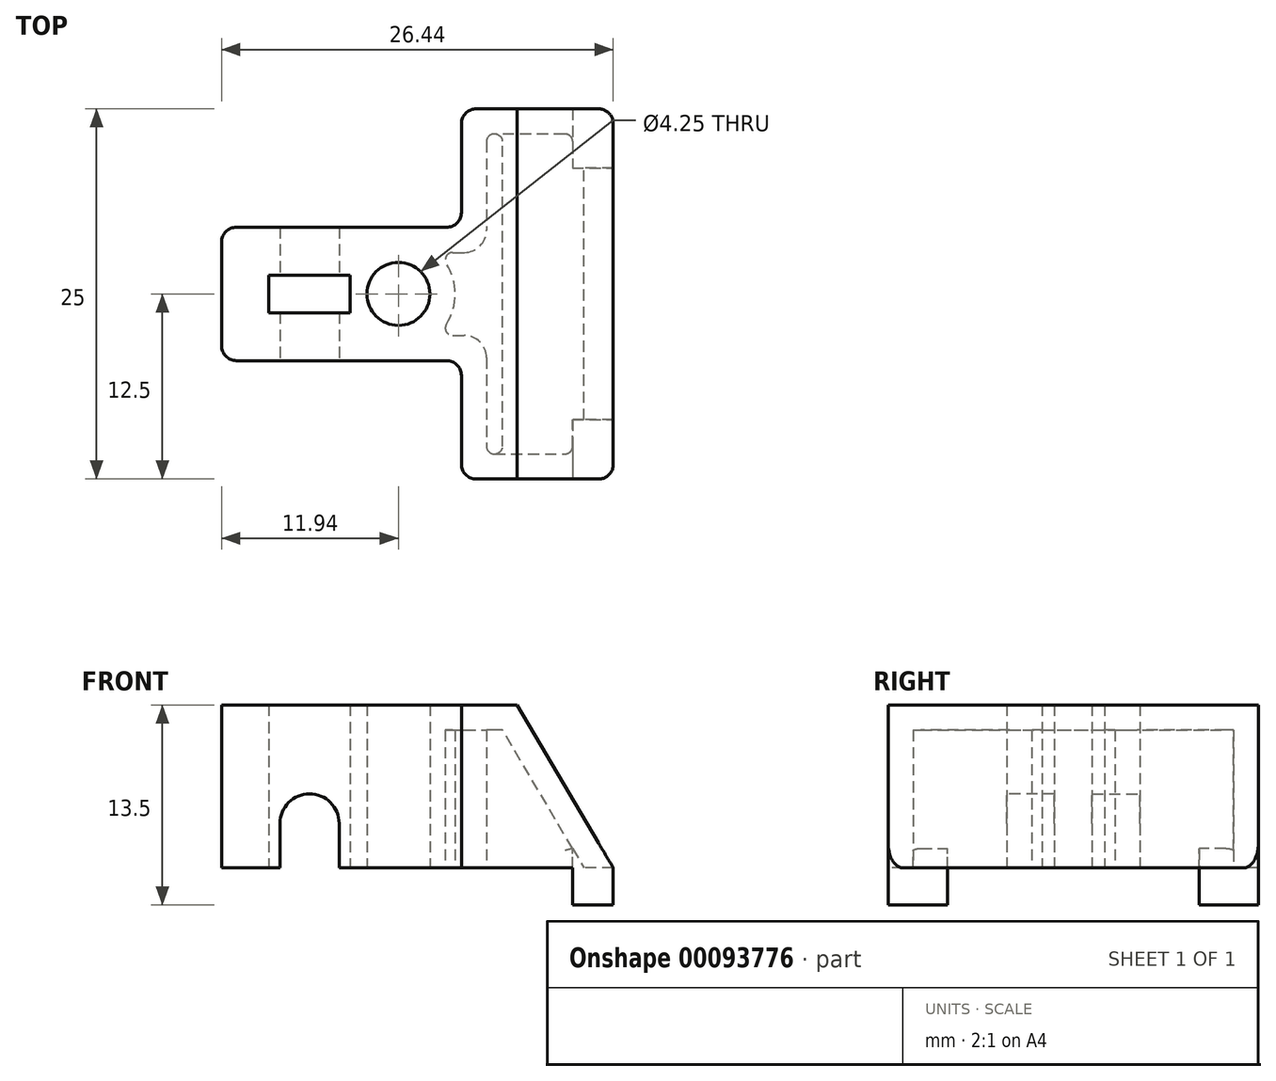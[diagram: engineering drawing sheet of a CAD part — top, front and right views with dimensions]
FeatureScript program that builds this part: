
annotation { "Feature Type Name" : "Feature", "Feature Type Description" : "" }
export const myFeature = defineFeature(function(context is Context, id is Id, definition is map)
    precondition{}
    {
        {
            var Q0;
            Q0=qCreatedBy(makeId("Top.planeOp"),FACE);
            var sketch = newSketch(context, id + "F0", { "sketchPlane" : qUnion([Q0])});
            skCircle(sketch, "E0", {"center": v(0, 0) * mm, "radius": 2.12 * mm});
            skLineSegment(sketch, "E1.bottom", {"start": v(-3.25, 1.27) * mm, "end": v(-8.75, 1.27) * mm});
            skLineSegment(sketch, "E1.top", {"start": v(-3.25, -1.27) * mm, "end": v(-8.75, -1.27) * mm});
            skLineSegment(sketch, "E1.left", {"start": v(-3.25, 1.27) * mm, "end": v(-3.25, -1.27) * mm});
            skLineSegment(sketch, "E1.right", {"start": v(-8.75, 1.27) * mm, "end": v(-8.75, -1.27) * mm});
            skPoint(sketch, "E1.middle", {"position": v(-6, 0) * mm});
            skLineSegment(sketch, "E2.bottom", {"start": v(-8, 4.5) * mm, "end": v(-4, 4.5) * mm});
            skLineSegment(sketch, "E2.top", {"start": v(-8, -4.5) * mm, "end": v(-4, -4.5) * mm});
            skLineSegment(sketch, "E2.left", {"start": v(-8, 4.5) * mm, "end": v(-8, -4.5) * mm});
            skLineSegment(sketch, "E2.right", {"start": v(-4, 4.5) * mm, "end": v(-4, -4.5) * mm});
            skLineSegment(sketch, "E3.bottom", {"start": v(-11.94, 4.5) * mm, "end": v(11.75, 4.5) * mm});
            skLineSegment(sketch, "E3.top", {"start": v(-11.94, -4.5) * mm, "end": v(11.75, -4.5) * mm});
            skLineSegment(sketch, "E3.left", {"start": v(-11.94, 4.5) * mm, "end": v(-11.94, -4.5) * mm});
            skLineSegment(sketch, "E3.right", {"start": v(11.75, 4.5) * mm, "end": v(11.75, -4.5) * mm});
            skLineSegment(sketch, "E4.bottom", {"start": v(11.75, 12.5) * mm, "end": v(4.25, 12.5) * mm});
            skLineSegment(sketch, "E4.top", {"start": v(11.75, -12.5) * mm, "end": v(4.25, -12.5) * mm});
            skLineSegment(sketch, "E4.left", {"start": v(11.75, 12.5) * mm, "end": v(11.75, -12.5) * mm});
            skLineSegment(sketch, "E4.right", {"start": v(4.25, 12.5) * mm, "end": v(4.25, -12.5) * mm});
            skPoint(sketch, "E4.middle", {"position": v(8, 0) * mm});
            skSolve(sketch);
        }
        {
            var Q0;
            {var subQ5=sQuery(id+"F0.wireOp",EDGE,"E4.bottom");Q0=makeQuery(id+"F0.imprint","IMPRINT",FACE,{"disambiguationData":[TD([[makeQuery(id+"F0.imprint","IMPRINT",EDGE,{"derivedFrom":subQ5}),1.0]])]});}
            var Q1;
            {var subQ0=sQuery(id+"F0.wireOp",EDGE,"E4.left");var subQ1=sQuery(id+"F0.wireOp",EDGE,"E3.bottom");var subQ2=makeQuery(id+"F0.imprint","INTERSECT",VERTEX,{"derivedFrom":[subQ1,subQ0]});Q1=makeQuery(id+"F0.imprint","IMPRINT",FACE,{"disambiguationData":[TD([[makeQuery(id+"F0.imprint","IMPRINT",EDGE,{"disambiguationData":[TD([[subQ2,1.0]])],"derivedFrom":subQ1}),-1.0]])]});}
            var Q2;
            {var subQ5=sQuery(id+"F0.wireOp",EDGE,"E4.top");Q2=makeQuery(id+"F0.imprint","IMPRINT",FACE,{"disambiguationData":[TD([[makeQuery(id+"F0.imprint","IMPRINT",EDGE,{"derivedFrom":subQ5}),-1.0]])]});}
            var Q3;
            Q3=makeQuery(id+"F0.imprint","IMPRINT",FACE,{"disambiguationData":[TD([[makeQuery(id+"F0.imprint","IMPRINT",EDGE,{"derivedFrom":sQuery(id+"F0.wireOp",EDGE,"E0")}),-1.0]])]});
            var Q4;
            {var subQ6=sQuery(id+"F0.wireOp",EDGE,"E1.right");Q4=makeQuery(id+"F0.imprint","IMPRINT",FACE,{"disambiguationData":[TD([[makeQuery(id+"F0.imprint","IMPRINT",EDGE,{"derivedFrom":subQ6}),-1.0]])]});}
            var Q5;
            {var subQ0=sQuery(id+"F0.wireOp",EDGE,"E2.right");var subQ1=sQuery(id+"F0.wireOp",EDGE,"E1.bottom");var subQ2=makeQuery(id+"F0.imprint","INTERSECT",VERTEX,{"derivedFrom":[subQ1,subQ0]});Q5=makeQuery(id+"F0.imprint","IMPRINT",FACE,{"disambiguationData":[TD([[makeQuery(id+"F0.imprint","IMPRINT",EDGE,{"disambiguationData":[TD([[subQ2,-1.0]])],"derivedFrom":subQ1}),-1.0]])]});}
            var Q6;
            {var subQ0=sQuery(id+"F0.wireOp",EDGE,"E2.right");var subQ1=sQuery(id+"F0.wireOp",EDGE,"E1.top");var subQ2=makeQuery(id+"F0.imprint","INTERSECT",VERTEX,{"derivedFrom":[subQ1,subQ0]});Q6=makeQuery(id+"F0.imprint","IMPRINT",FACE,{"disambiguationData":[TD([[makeQuery(id+"F0.imprint","IMPRINT",EDGE,{"disambiguationData":[TD([[subQ2,-1.0]])],"derivedFrom":subQ1}),1.0]])]});}
            extrude(context, id + "F1", {"entities" : qUnion([Q0, Q1, Q2, Q3, Q4, Q5, Q6]), "depth" : 11 * mm});
        }
        {
            var Q0;
            {var subQ0=sQuery(id+"F0.wireOp",EDGE,"E2.right");var subQ1=sQuery(id+"F0.wireOp",EDGE,"E1.bottom");var subQ2=makeQuery(id+"F0.imprint","INTERSECT",VERTEX,{"derivedFrom":[subQ1,subQ0]});Q0=makeQuery(id+"F0.imprint","IMPRINT",FACE,{"disambiguationData":[TD([[makeQuery(id+"F0.imprint","IMPRINT",EDGE,{"disambiguationData":[TD([[subQ2,-1.0]])],"derivedFrom":subQ1}),-1.0]])]});}
            var Q1;
            {var subQ0=sQuery(id+"F0.wireOp",EDGE,"E2.right");var subQ1=sQuery(id+"F0.wireOp",EDGE,"E1.top");var subQ2=makeQuery(id+"F0.imprint","INTERSECT",VERTEX,{"derivedFrom":[subQ1,subQ0]});Q1=makeQuery(id+"F0.imprint","IMPRINT",FACE,{"disambiguationData":[TD([[makeQuery(id+"F0.imprint","IMPRINT",EDGE,{"disambiguationData":[TD([[subQ2,-1.0]])],"derivedFrom":subQ1}),1.0]])]});}
            extrude(context, id + "F2", {"entities" : qUnion([Q0, Q1]), "operationType" : NewBodyOperationType.REMOVE, "depth" : 5 * mm});
        }
        {
            var Q0;
            {var subQ0=sQuery(id+"F0.wireOp",EDGE,"E4.right");var subQ1=sQuery(id+"F0.wireOp",EDGE,"E4.bottom");var subQ2=sQuery(id+"F0.wireOp",EDGE,"E3.bottom");var subQ3=sQuery(id+"F0.wireOp",EDGE,"E4.top");var subQ4=sQuery(id+"F0.wireOp",EDGE,"E3.top");var subQ5=sQuery(id+"F0.wireOp",EDGE,"E0");var subQ6=sQuery(id+"F0.wireOp",EDGE,"E1.bottom");var subQ7=sQuery(id+"F0.wireOp",EDGE,"E1.top");var subQ8=sQuery(id+"F0.wireOp",EDGE,"E4.left");var subQ9=sQuery(id+"F0.wireOp",EDGE,"E1.left");Q0=makeQuery(id+"F2.boolean.opBoolean","SPLIT",FACE,{"disambiguationData":[TD([makeQuery(id+"F1.opExtrude","SWEPT_FACE",FACE,{"disambiguationData":[OSD([subQ5])]})])],"derivedFrom":makeQuery(id+"F1.opExtrude","CAP_FACE",FACE,{"disambiguationData":[OSD([subQ5,subQ6,subQ7,subQ9,sQuery(id+"F0.wireOp",EDGE,"E1.right"),subQ2,subQ4,sQuery(id+"F0.wireOp",EDGE,"E3.left"),subQ1,subQ3,subQ8,subQ0])],"isStart":true})});}
            var sketch = newSketch(context, id + "F3", { "sketchPlane" : qUnion([Q0])});
            skLineSegment(sketch, "E5.bottom", {"start": v(11.75, -12.5) * mm, "end": v(14.5, -12.5) * mm});
            skLineSegment(sketch, "E5.top", {"start": v(11.75, -8.5) * mm, "end": v(14.5, -8.5) * mm});
            skLineSegment(sketch, "E5.left", {"start": v(11.75, -12.5) * mm, "end": v(11.75, -8.5) * mm});
            skLineSegment(sketch, "E5.right", {"start": v(14.5, -12.5) * mm, "end": v(14.5, -8.5) * mm});
            skLineSegment(sketch, "E6", {"start": v(0, 0) * mm, "end": v(11.75, 0) * mm});
            skLineSegment(sketch, "E7.MirrorCS", {"start": v(11.75, 8.5) * mm, "end": v(14.5, 8.5) * mm});
            skLineSegment(sketch, "E8.MirrorCS", {"start": v(14.5, 12.5) * mm, "end": v(14.5, 8.5) * mm});
            skLineSegment(sketch, "E9.MirrorCS", {"start": v(11.75, 12.5) * mm, "end": v(14.5, 12.5) * mm});
            skLineSegment(sketch, "E10.MirrorCS", {"start": v(11.75, 12.5) * mm, "end": v(11.75, 8.5) * mm});
            skSolve(sketch);
        }
        {
            var Q0;
            {var subQ0=sQuery(id+"F0.wireOp",EDGE,"E2.right");Q0=makeQuery(id+"F2.boolean.opBoolean","COPY",EDGE,{"derivedFrom":makeQuery(id+"F2.opExtrude","CAP_EDGE",EDGE,{"disambiguationData":[OSD([subQ0]),TDD([makeQuery(id+"F0.imprint","IMPRINT",EDGE,{"disambiguationData":[TD([[makeQuery(id+"F0.imprint","INTERSECT",VERTEX,{"derivedFrom":[subQ0,sQuery(id+"F0.wireOp",EDGE,"E3.bottom")]}),-1.0]])],"derivedFrom":subQ0})])],"isStart":false})});}
            var Q1;
            {var subQ0=sQuery(id+"F0.wireOp",EDGE,"E2.left");Q1=makeQuery(id+"F2.boolean.opBoolean","COPY",EDGE,{"derivedFrom":makeQuery(id+"F2.opExtrude","CAP_EDGE",EDGE,{"disambiguationData":[OSD([subQ0]),TDD([makeQuery(id+"F0.imprint","IMPRINT",EDGE,{"disambiguationData":[TD([[makeQuery(id+"F0.imprint","INTERSECT",VERTEX,{"derivedFrom":[subQ0,sQuery(id+"F0.wireOp",EDGE,"E3.bottom")]}),-1.0]])],"derivedFrom":subQ0})])],"isStart":false})});}
            var Q2;
            {var subQ0=sQuery(id+"F0.wireOp",EDGE,"E2.left");Q2=makeQuery(id+"F2.boolean.opBoolean","COPY",EDGE,{"derivedFrom":makeQuery(id+"F2.opExtrude","CAP_EDGE",EDGE,{"disambiguationData":[OSD([subQ0]),TDD([makeQuery(id+"F0.imprint","IMPRINT",EDGE,{"disambiguationData":[TD([[makeQuery(id+"F0.imprint","INTERSECT",VERTEX,{"derivedFrom":[subQ0,sQuery(id+"F0.wireOp",EDGE,"E3.top")]}),1.0]])],"derivedFrom":subQ0})])],"isStart":false})});}
            var Q3;
            {var subQ0=sQuery(id+"F0.wireOp",EDGE,"E2.right");Q3=makeQuery(id+"F2.boolean.opBoolean","COPY",EDGE,{"derivedFrom":makeQuery(id+"F2.opExtrude","CAP_EDGE",EDGE,{"disambiguationData":[OSD([subQ0]),TDD([makeQuery(id+"F0.imprint","IMPRINT",EDGE,{"disambiguationData":[TD([[makeQuery(id+"F0.imprint","INTERSECT",VERTEX,{"derivedFrom":[subQ0,sQuery(id+"F0.wireOp",EDGE,"E3.top")]}),1.0]])],"derivedFrom":subQ0})])],"isStart":false})});}
            fillet(context, id + "F4", {"entities" : qUnion([Q0, Q1, Q2, Q3]), "radius" : 2 * mm, "tangentPropagation" : true, "allowEdgeOverflow" : false});
        }
        {
            var Q0;
            Q0=makeQuery(id+"F3.imprint","IMPRINT",FACE,{"disambiguationData":[TD([[makeQuery(id+"F3.imprint","IMPRINT",EDGE,{"derivedFrom":sQuery(id+"F3.wireOp",EDGE,"E5.bottom")}),1.0]])]});
            var Q1;
            Q1=makeQuery(id+"F3.imprint","IMPRINT",FACE,{"disambiguationData":[TD([[makeQuery(id+"F3.imprint","IMPRINT",EDGE,{"derivedFrom":sQuery(id+"F3.wireOp",EDGE,"E7.MirrorCS")}),1.0]])]});
            extrude(context, id + "F5", {"entities" : qUnion([Q0, Q1]), "operationType" : NewBodyOperationType.ADD, "depth" : 5 * mm, "symmetric" : true});
        }
        {
            var Q0;
            Q0=makeQuery(id+"F5.boolean.opBoolean","MERGE",FACE,{"derivedFrom":[makeQuery(id+"F1.opExtrude","SWEPT_FACE",FACE,{"disambiguationData":[OSD([sQuery(id+"F0.wireOp",EDGE,"E4.bottom")])]}),makeQuery(id+"F5.opExtrude","SWEPT_FACE",FACE,{"disambiguationData":[OSD([sQuery(id+"F3.wireOp",EDGE,"E5.bottom")])]})]});
            var sketch = newSketch(context, id + "F6", { "sketchPlane" : qUnion([Q0])});
            skLineSegment(sketch, "E11", {"start": v(-11.75, 0) * mm, "end": v(-14.5, 0) * mm});
            skLineSegment(sketch, "E12", {"start": v(-14.5, 0) * mm, "end": v(-8, 11) * mm});
            skSolve(sketch);
        }
        {
            var Q0;
            {var subQ0=sQuery(id+"F6.wireOp",EDGE,"E12");var subQ1=sQuery(id+"F0.wireOp",EDGE,"E4.bottom");var subQ2=makeQuery(id+"F1.opExtrude","CAP_EDGE",EDGE,{"disambiguationData":[OSD([subQ1])],"isStart":false});var subQ3=makeQuery(id+"F6.imprint","INTERSECT",VERTEX,{"derivedFrom":[subQ2,subQ0]});Q0=makeQuery(id+"F6.imprint","IMPRINT",FACE,{"disambiguationData":[TD([[makeQuery(id+"F6.imprint","IMPRINT",EDGE,{"disambiguationData":[TD([[subQ3,1.0]])],"derivedFrom":subQ0}),1.0]])]});}
            var Q1;
            {var subQ0=sQuery(id+"F6.wireOp",EDGE,"E12");var subQ1=sQuery(id+"F3.wireOp",EDGE,"E5.bottom");var subQ4=makeQuery(id+"F5.opExtrude","CAP_EDGE",EDGE,{"disambiguationData":[OSD([subQ1])],"isStart":true});var subQ5=makeQuery(id+"F6.imprint","INTERSECT",VERTEX,{"derivedFrom":[subQ4,subQ0]});Q1=makeQuery(id+"F6.imprint","IMPRINT",FACE,{"disambiguationData":[TD([[makeQuery(id+"F6.imprint","IMPRINT",EDGE,{"disambiguationData":[TD([[subQ5,-1.0]])],"derivedFrom":subQ4}),1.0]])]});}
            extrude(context, id + "F7", {"entities" : qUnion([Q0, Q1]), "operationType" : NewBodyOperationType.REMOVE, "endBound" : BoundingType.THROUGH_ALL, "oppositeDirection" : true, "depth" : 25 * mm});
        }
        {
            var Q0;
            {var subQ0=sQuery(id+"F6.wireOp",EDGE,"E12");var subQ1=makeQuery(id+"F5.opExtrude","CAP_EDGE",EDGE,{"disambiguationData":[OSD([sQuery(id+"F3.wireOp",EDGE,"E5.bottom")])],"isStart":true});var subQ2=makeQuery(id+"F6.imprint","INTERSECT",VERTEX,{"derivedFrom":[subQ1,subQ0]});Q0=makeQuery(id+"F6.imprint","IMPRINT",FACE,{"disambiguationData":[TD([[makeQuery(id+"F6.imprint","IMPRINT",EDGE,{"disambiguationData":[TD([[subQ2,-1.0]])],"derivedFrom":subQ0}),-1.0]])]});}
            var Q1;
            {var subQ7=sQuery(id+"F6.wireOp",EDGE,"E11");Q1=makeQuery(id+"F6.imprint","IMPRINT",FACE,{"disambiguationData":[TD([[makeQuery(id+"F6.imprint","IMPRINT",EDGE,{"derivedFrom":subQ7}),-1.0]])]});}
            var Q2;
            Q2=makeQuery(id+"F5.boolean.opBoolean","MERGE",FACE,{"derivedFrom":[makeQuery(id+"F1.opExtrude","SWEPT_FACE",FACE,{"disambiguationData":[OSD([sQuery(id+"F0.wireOp",EDGE,"E4.top")])]}),makeQuery(id+"F5.opExtrude","SWEPT_FACE",FACE,{"disambiguationData":[OSD([sQuery(id+"F3.wireOp",EDGE,"E9.MirrorCS")])]})]});
            extrude(context, id + "F8", {"entities" : qUnion([Q0, Q1]), "operationType" : NewBodyOperationType.ADD, "endBound" : BoundingType.UP_TO_SURFACE, "oppositeDirection" : true, "endBoundEntityFace" : qUnion([Q2]), "depth" : 25 * mm});
        }
        {
            var Q0;
            {var subQ0=sQuery(id+"F0.wireOp",EDGE,"E4.bottom");var subQ1=sQuery(id+"F0.wireOp",EDGE,"E4.right");var subQ2=sQuery(id+"F0.wireOp",EDGE,"E3.bottom");var subQ3=sQuery(id+"F0.wireOp",EDGE,"E4.left");var subQ4=sQuery(id+"F0.wireOp",EDGE,"E3.top");var subQ5=sQuery(id+"F0.wireOp",EDGE,"E4.top");var subQ6=sQuery(id+"F0.wireOp",EDGE,"E0");var subQ7=sQuery(id+"F0.wireOp",EDGE,"E1.left");var subQ8=sQuery(id+"F0.wireOp",EDGE,"E1.bottom");var subQ9=sQuery(id+"F0.wireOp",EDGE,"E1.top");Q0=makeQuery(id+"F8.boolean.opBoolean","MERGE",FACE,{"derivedFrom":[makeQuery(id+"F2.boolean.opBoolean","SPLIT",FACE,{"disambiguationData":[TD([makeQuery(id+"F1.opExtrude","SWEPT_FACE",FACE,{"disambiguationData":[OSD([subQ6])]})])],"derivedFrom":makeQuery(id+"F1.opExtrude","CAP_FACE",FACE,{"disambiguationData":[OSD([subQ6,subQ8,subQ9,subQ7,sQuery(id+"F0.wireOp",EDGE,"E1.right"),subQ2,subQ4,sQuery(id+"F0.wireOp",EDGE,"E3.left"),subQ0,subQ5,subQ3,subQ1])],"isStart":true})}),makeQuery(id+"F8.opExtrude","SWEPT_FACE",FACE,{"disambiguationData":[OSD([subQ0,sQuery(id+"F6.wireOp",EDGE,"E11")])]})]});}
            shell(context, id + "F9", {"entities" : qUnion([Q0]), "thickness" : 1.7 * mm});
        }
        {
            var Q0;
            Q0=makeQuery(id+"F5.opExtrude","CAP_FACE",FACE,{"disambiguationData":[OSD([sQuery(id+"F3.wireOp",EDGE,"E7.MirrorCS"),sQuery(id+"F3.wireOp",EDGE,"E8.MirrorCS"),sQuery(id+"F3.wireOp",EDGE,"E9.MirrorCS"),sQuery(id+"F3.wireOp",EDGE,"E10.MirrorCS")])],"isStart":false});
            var sketch = newSketch(context, id + "F10", { "sketchPlane" : qUnion([Q0])});
            skLineSegment(sketch, "E13.0.0", {"start": v(11.75, -8.5) * mm, "end": v(11.75, -12.5) * mm});
            skLineSegment(sketch, "E13.0.1", {"start": v(11.75, -12.5) * mm, "end": v(14.5, -12.5) * mm});
            skLineSegment(sketch, "E13.0.2", {"start": v(14.5, -12.5) * mm, "end": v(14.5, -8.5) * mm});
            skLineSegment(sketch, "E13.0.3", {"start": v(14.5, -8.5) * mm, "end": v(11.75, -8.5) * mm});
            skSolve(sketch);
        }
        {
            var Q0;
            Q0=makeQuery(id+"F10.imprint","IMPRINT",FACE,{"disambiguationData":[TD([[makeQuery(id+"F10.imprint","IMPRINT",EDGE,{"derivedFrom":makeQuery(id+"F5.opExtrude","CAP_EDGE",EDGE,{"disambiguationData":[OSD([sQuery(id+"F3.wireOp",EDGE,"E7.MirrorCS")])],"isStart":false})}),1.0]])]});
            var Q1;
            Q1=makeQuery(id+"F10.imprint","IMPRINT",FACE,{"disambiguationData":[TD([[makeQuery(id+"F10.imprint","IMPRINT",EDGE,{"derivedFrom":sQuery(id+"F10.wireOp",EDGE,"E13.0.0")}),1.0]])]});
            var Q2;
            Q2=makeQuery(id+"F9.opShell","OFFSET_FACE",FACE,{"disambiguationData":[OSD([sQuery(id+"F6.wireOp",EDGE,"E12")])]});
            extrude(context, id + "F11", {"entities" : qUnion([Q0, Q1]), "operationType" : NewBodyOperationType.ADD, "endBound" : BoundingType.UP_TO_SURFACE, "oppositeDirection" : true, "endBoundEntityFace" : qUnion([Q2]), "depth" : 25 * mm});
        }
        {
            var Q0;
            Q0=makeQuery(id+"F5.opExtrude","SWEPT_EDGE",EDGE,{"disambiguationData":[OSD([sQuery(id+"F3.wireOp",EDGE,"E5.bottom"),sQuery(id+"F3.wireOp",EDGE,"E5.right")])]});
            var Q1;
            Q1=makeQuery(id+"F5.opExtrude","SWEPT_EDGE",EDGE,{"disambiguationData":[OSD([sQuery(id+"F3.wireOp",EDGE,"E8.MirrorCS"),sQuery(id+"F3.wireOp",EDGE,"E9.MirrorCS")])]});
            var Q2;
            Q2=makeQuery(id+"F1.opExtrude","SWEPT_EDGE",EDGE,{"disambiguationData":[OSD([sQuery(id+"F0.wireOp",EDGE,"E4.top"),sQuery(id+"F0.wireOp",EDGE,"E4.right")])]});
            var Q3;
            Q3=makeQuery(id+"F1.opExtrude","SWEPT_EDGE",EDGE,{"disambiguationData":[OSD([sQuery(id+"F0.wireOp",EDGE,"E4.bottom"),sQuery(id+"F0.wireOp",EDGE,"E4.right")])]});
            var Q4;
            Q4=makeQuery(id+"F1.opExtrude","SWEPT_EDGE",EDGE,{"disambiguationData":[OSD([sQuery(id+"F0.wireOp",EDGE,"E3.bottom"),sQuery(id+"F0.wireOp",EDGE,"E3.left")])]});
            var Q5;
            Q5=makeQuery(id+"F1.opExtrude","SWEPT_EDGE",EDGE,{"disambiguationData":[OSD([sQuery(id+"F0.wireOp",EDGE,"E3.top"),sQuery(id+"F0.wireOp",EDGE,"E3.left")])]});
            var Q6;
            Q6=makeQuery(id+"F1.opExtrude","SWEPT_EDGE",EDGE,{"disambiguationData":[OSD([sQuery(id+"F0.wireOp",EDGE,"E3.top"),sQuery(id+"F0.wireOp",EDGE,"E4.right")])]});
            var Q7;
            Q7=makeQuery(id+"F1.opExtrude","SWEPT_EDGE",EDGE,{"disambiguationData":[OSD([sQuery(id+"F0.wireOp",EDGE,"E3.bottom"),sQuery(id+"F0.wireOp",EDGE,"E4.right")])]});
            fillet(context, id + "F12", {"entities" : qUnion([Q0, Q1, Q2, Q3, Q4, Q5, Q6, Q7]), "radius" : 1 * mm, "tangentPropagation" : true, "allowEdgeOverflow" : false});
        }
        {
            var Q0;
            Q0=makeQuery(id+"F9.opShell","TWEAK_EDGE",EDGE,{"derivedFrom":[makeQuery(id+"F1.opExtrude","SWEPT_FACE",FACE,{"disambiguationData":[OSD([sQuery(id+"F0.wireOp",EDGE,"E0")])]}),makeQuery(id+"F1.opExtrude","SWEPT_FACE",FACE,{"disambiguationData":[OSD([sQuery(id+"F0.wireOp",EDGE,"E3.top")])]})]});
            var Q1;
            Q1=makeQuery(id+"F9.opShell","OFFSET_EDGE",EDGE,{"disambiguationData":[OSD([sQuery(id+"F0.wireOp",EDGE,"E4.top"),sQuery(id+"F0.wireOp",EDGE,"E4.right")])]});
            var Q2;
            Q2=makeQuery(id+"F9.opShell","OFFSET_EDGE",EDGE,{"disambiguationData":[OSD([sQuery(id+"F0.wireOp",EDGE,"E4.bottom"),sQuery(id+"F0.wireOp",EDGE,"E4.right")])]});
            var Q3;
            Q3=makeQuery(id+"F9.opShell","TWEAK_EDGE",EDGE,{"derivedFrom":[makeQuery(id+"F1.opExtrude","SWEPT_FACE",FACE,{"disambiguationData":[OSD([sQuery(id+"F0.wireOp",EDGE,"E0")])]}),makeQuery(id+"F1.opExtrude","SWEPT_FACE",FACE,{"disambiguationData":[OSD([sQuery(id+"F0.wireOp",EDGE,"E3.bottom")])]})]});
            var Q4;
            Q4=makeQuery(id+"F9.opShell","OFFSET_EDGE",EDGE,{"disambiguationData":[OSD([sQuery(id+"F0.wireOp",EDGE,"E4.top"),sQuery(id+"F3.wireOp",EDGE,"E9.MirrorCS"),sQuery(id+"F6.wireOp",EDGE,"E12")])]});
            var Q5;
            Q5=makeQuery(id+"F9.opShell","OFFSET_EDGE",EDGE,{"disambiguationData":[OSD([sQuery(id+"F0.wireOp",EDGE,"E4.bottom"),sQuery(id+"F6.wireOp",EDGE,"E12")])]});
            var Q6;
            Q6=makeQuery(id+"F11.boolean.opBoolean","INTERSECT",EDGE,{"derivedFrom":[makeQuery(id+"F9.opShell","OFFSET_FACE",FACE,{"disambiguationData":[OSD([sQuery(id+"F0.wireOp",EDGE,"E4.bottom"),sQuery(id+"F0.wireOp",EDGE,"E4.top"),sQuery(id+"F0.wireOp",EDGE,"E4.right"),sQuery(id+"F3.wireOp",EDGE,"E9.MirrorCS"),sQuery(id+"F6.wireOp",EDGE,"E11"),sQuery(id+"F6.wireOp",EDGE,"E12")])]}),makeQuery(id+"F11.opExtrude","SWEPT_FACE",FACE,{"disambiguationData":[OSD([sQuery(id+"F3.wireOp",EDGE,"E10.MirrorCS")])]})]});
            var Q7;
            Q7=makeQuery(id+"F9.opShell","OFFSET_EDGE",EDGE,{"disambiguationData":[OSD([sQuery(id+"F6.wireOp",EDGE,"E12")])]});
            var Q8;
            Q8=makeQuery(id+"F11.boolean.opBoolean","INTERSECT",EDGE,{"derivedFrom":[makeQuery(id+"F9.opShell","OFFSET_FACE",FACE,{"disambiguationData":[OSD([sQuery(id+"F0.wireOp",EDGE,"E4.bottom"),sQuery(id+"F0.wireOp",EDGE,"E4.right"),sQuery(id+"F3.wireOp",EDGE,"E5.bottom"),sQuery(id+"F6.wireOp",EDGE,"E11"),sQuery(id+"F6.wireOp",EDGE,"E12")])]}),makeQuery(id+"F11.opExtrude","SWEPT_FACE",FACE,{"disambiguationData":[OSD([sQuery(id+"F10.wireOp",EDGE,"E13.0.0")])]})]});
            fillet(context, id + "F13", {"entities" : qUnion([Q0, Q1, Q2, Q3, Q4, Q5, Q6, Q7, Q8]), "radius" : 0.5 * mm, "tangentPropagation" : true, "allowEdgeOverflow" : false});
        }
        {
            var Q0;
            Q0=makeQuery(id+"F9.opShell","OFFSET_EDGE",EDGE,{"disambiguationData":[OSD([sQuery(id+"F0.wireOp",EDGE,"E3.top"),sQuery(id+"F0.wireOp",EDGE,"E4.right")])]});
            var Q1;
            Q1=makeQuery(id+"F9.opShell","OFFSET_EDGE",EDGE,{"disambiguationData":[OSD([sQuery(id+"F0.wireOp",EDGE,"E3.bottom"),sQuery(id+"F0.wireOp",EDGE,"E4.right")])]});
            fillet(context, id + "F14", {"entities" : qUnion([Q0, Q1]), "radius" : 1.5 * mm, "tangentPropagation" : true, "allowEdgeOverflow" : false});
        }
    });
